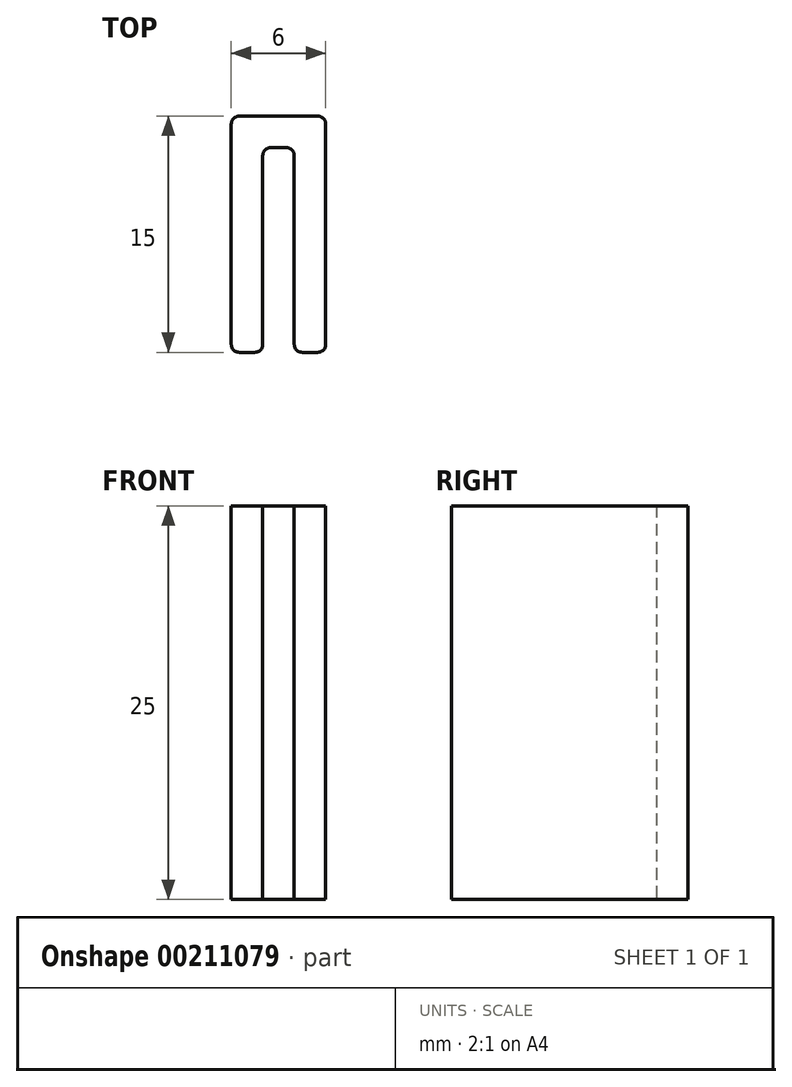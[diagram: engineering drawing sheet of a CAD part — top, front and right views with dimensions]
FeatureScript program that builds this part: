
annotation { "Feature Type Name" : "Feature", "Feature Type Description" : "" }
export const myFeature = defineFeature(function(context is Context, id is Id, definition is map)
    precondition{}
    {
        {
            var Q0;
            Q0=qCreatedBy(makeId("Top.planeOp"),FACE);
            var sketch = newSketch(context, id + "F0", { "sketchPlane" : qUnion([Q0])});
            skLineSegment(sketch, "E0.bottom", {"start": v(0, 0) * mm, "end": v(2, 0) * mm});
            skLineSegment(sketch, "E0.top", {"start": v(0, -15) * mm, "end": v(2, -15) * mm});
            skLineSegment(sketch, "E0.left", {"start": v(0, 0) * mm, "end": v(0, -15) * mm});
            skLineSegment(sketch, "E0.right", {"start": v(2, 0) * mm, "end": v(2, -15) * mm});
            skLineSegment(sketch, "E1.bottom", {"start": v(2, 0) * mm, "end": v(4, 0) * mm});
            skLineSegment(sketch, "E1.top", {"start": v(2, -2) * mm, "end": v(4, -2) * mm});
            skLineSegment(sketch, "E1.left", {"start": v(2, 0) * mm, "end": v(2, -2) * mm});
            skLineSegment(sketch, "E1.right", {"start": v(4, 0) * mm, "end": v(4, -2) * mm});
            skLineSegment(sketch, "E2.bottom", {"start": v(4, 0) * mm, "end": v(6, 0) * mm});
            skLineSegment(sketch, "E2.top", {"start": v(4, -15) * mm, "end": v(6, -15) * mm});
            skLineSegment(sketch, "E2.left", {"start": v(4, 0) * mm, "end": v(4, -15) * mm});
            skLineSegment(sketch, "E2.right", {"start": v(6, 0) * mm, "end": v(6, -15) * mm});
            skSolve(sketch);
        }
        {
            var Q0;
            Q0 = qSketchRegion(id + "F0", true);
            extrude(context, id + "F1", {"entities" : qUnion([Q0]), "depth" : 25 * mm});
        }
        {
            var Q0;
            Q0=makeQuery(id+"F1.opExtrude","SWEPT_EDGE",EDGE,{"disambiguationData":[OSD([sQuery(id+"F0.wireOp",EDGE,"E0.right"),sQuery(id+"F0.wireOp",EDGE,"E1.top"),sQuery(id+"F0.wireOp",EDGE,"E1.left")])]});
            var Q1;
            Q1=makeQuery(id+"F1.opExtrude","SWEPT_EDGE",EDGE,{"disambiguationData":[OSD([sQuery(id+"F0.wireOp",EDGE,"E1.top"),sQuery(id+"F0.wireOp",EDGE,"E2.left")])]});
            var Q2;
            Q2=makeQuery(id+"F1.opExtrude","SWEPT_EDGE",EDGE,{"disambiguationData":[OSD([sQuery(id+"F0.wireOp",EDGE,"E0.bottom"),sQuery(id+"F0.wireOp",EDGE,"E0.left")])]});
            var Q3;
            Q3=makeQuery(id+"F1.opExtrude","SWEPT_EDGE",EDGE,{"disambiguationData":[OSD([sQuery(id+"F0.wireOp",EDGE,"E2.bottom"),sQuery(id+"F0.wireOp",EDGE,"E2.right")])]});
            var Q4;
            Q4=makeQuery(id+"F1.opExtrude","SWEPT_EDGE",EDGE,{"disambiguationData":[OSD([sQuery(id+"F0.wireOp",EDGE,"E0.top"),sQuery(id+"F0.wireOp",EDGE,"E0.left")])]});
            var Q5;
            Q5=makeQuery(id+"F1.opExtrude","SWEPT_EDGE",EDGE,{"disambiguationData":[OSD([sQuery(id+"F0.wireOp",EDGE,"E0.top"),sQuery(id+"F0.wireOp",EDGE,"E0.right")])]});
            var Q6;
            Q6=makeQuery(id+"F1.opExtrude","SWEPT_EDGE",EDGE,{"disambiguationData":[OSD([sQuery(id+"F0.wireOp",EDGE,"E2.top"),sQuery(id+"F0.wireOp",EDGE,"E2.left")])]});
            var Q7;
            Q7=makeQuery(id+"F1.opExtrude","SWEPT_EDGE",EDGE,{"disambiguationData":[OSD([sQuery(id+"F0.wireOp",EDGE,"E2.top"),sQuery(id+"F0.wireOp",EDGE,"E2.right")])]});
            fillet(context, id + "F2", {"entities" : qUnion([Q0, Q1, Q2, Q3, Q4, Q5, Q6, Q7]), "radius" : .5 * mm, "tangentPropagation" : true, "allowEdgeOverflow" : false});
        }
    });
